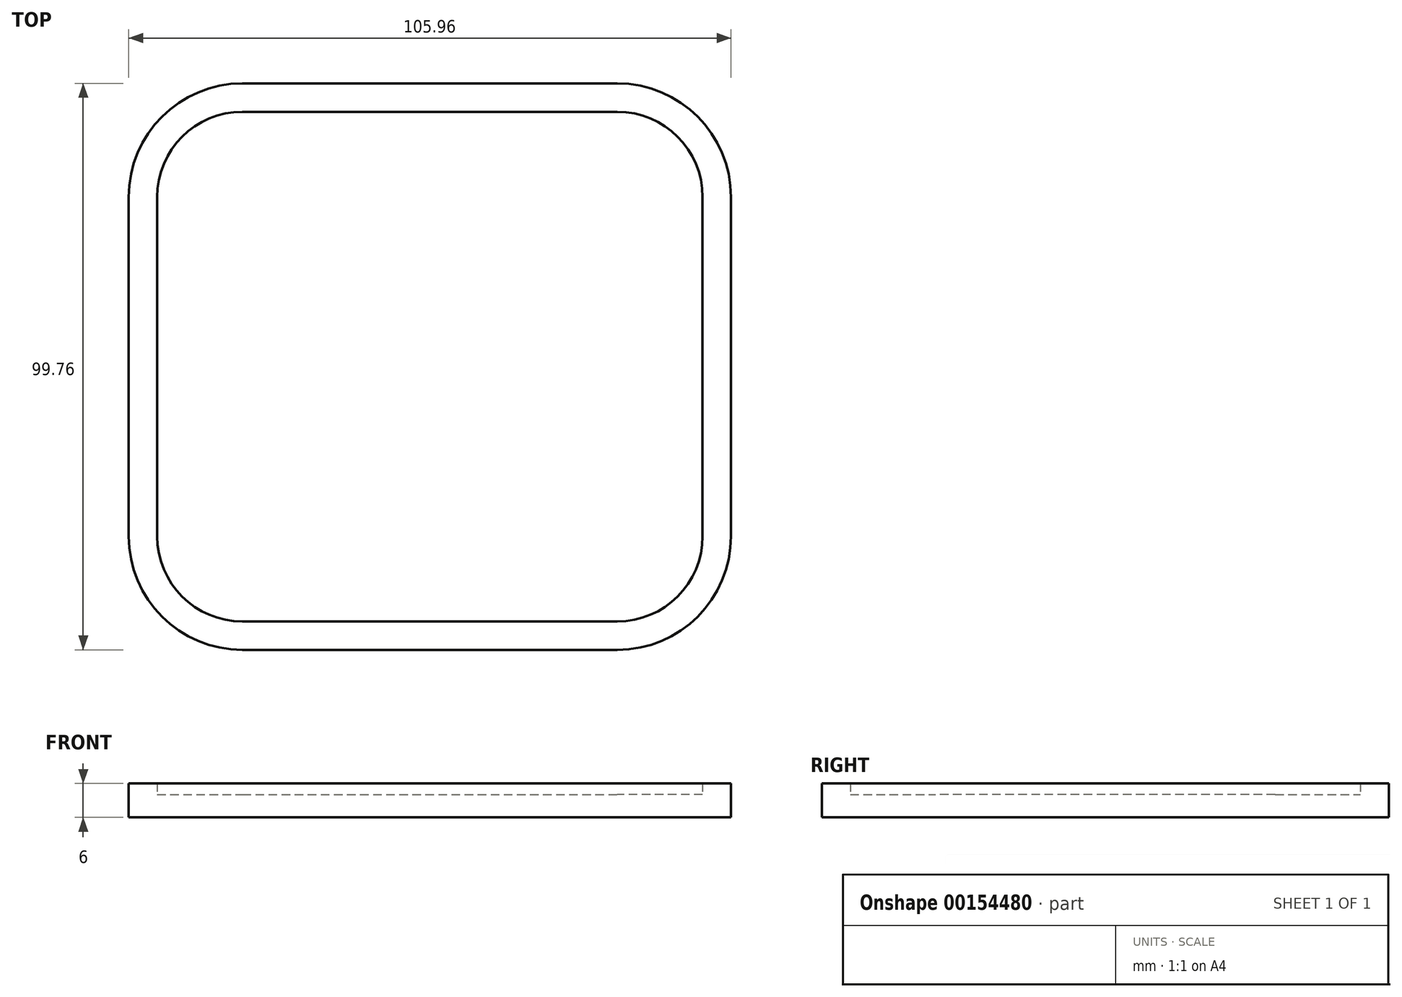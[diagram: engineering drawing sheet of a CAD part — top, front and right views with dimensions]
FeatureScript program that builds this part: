
annotation { "Feature Type Name" : "Feature", "Feature Type Description" : "" }
export const myFeature = defineFeature(function(context is Context, id is Id, definition is map)
    precondition{}
    {
        {
            var Q0;
            Q0=qCreatedBy(makeId("Top.planeOp"),FACE);
            var sketch = newSketch(context, id + "F0", { "sketchPlane" : qUnion([Q0])});
            skLineSegment(sketch, "E0.bottom", {"start": v(-32.98, 44.88) * mm, "end": v(32.98, 44.88) * mm});
            skLineSegment(sketch, "E0.top", {"start": v(-32.98, -44.88) * mm, "end": v(32.98, -44.88) * mm});
            skLineSegment(sketch, "E0.left", {"start": v(-47.98, 29.88) * mm, "end": v(-47.98, -29.88) * mm});
            skLineSegment(sketch, "E0.right", {"start": v(47.98, 29.88) * mm, "end": v(47.98, -29.88) * mm});
            skPoint(sketch, "E0.middle", {"position": v(0, 0) * mm});
            skPoint(sketch, "E1.visualSharp", {"position": v(-47.98, 44.88) * mm});
            skArc(sketch, "E1.filletArc", {"start": v(-32.98, 44.88) * mm, "mid": v(-43.59, 40.49) * mm, "end": v(-47.98, 29.88) * mm});
            skPoint(sketch, "E2.visualSharp", {"position": v(47.98, 44.88) * mm});
            skArc(sketch, "E2.filletArc", {"start": v(47.98, 29.88) * mm, "mid": v(43.59, 40.49) * mm, "end": v(32.98, 44.88) * mm});
            skPoint(sketch, "E3.visualSharp", {"position": v(47.98, -44.88) * mm});
            skArc(sketch, "E3.filletArc", {"start": v(32.98, -44.88) * mm, "mid": v(43.59, -40.49) * mm, "end": v(47.98, -29.88) * mm});
            skPoint(sketch, "E4.visualSharp", {"position": v(-47.98, -44.88) * mm});
            skArc(sketch, "E4.filletArc", {"start": v(-47.98, -29.88) * mm, "mid": v(-43.59, -40.49) * mm, "end": v(-32.98, -44.88) * mm});
            skLineSegment(sketch, "E5.0", {"start": v(-32.98, 49.88) * mm, "end": v(32.98, 49.88) * mm});
            skArc(sketch, "E5.1", {"start": v(52.98, 29.88) * mm, "mid": v(47.13, 44.02) * mm, "end": v(32.98, 49.88) * mm});
            skArc(sketch, "E5.2", {"start": v(-32.98, 49.88) * mm, "mid": v(-47.13, 44.02) * mm, "end": v(-52.98, 29.88) * mm});
            skLineSegment(sketch, "E5.3", {"start": v(52.98, 29.88) * mm, "end": v(52.98, -29.88) * mm});
            skLineSegment(sketch, "E5.4", {"start": v(-52.98, 29.88) * mm, "end": v(-52.98, -29.88) * mm});
            skArc(sketch, "E5.5", {"start": v(-52.98, -29.88) * mm, "mid": v(-47.13, -44.02) * mm, "end": v(-32.98, -49.88) * mm});
            skLineSegment(sketch, "E5.6", {"start": v(-32.98, -49.88) * mm, "end": v(32.98, -49.88) * mm});
            skArc(sketch, "E5.7", {"start": v(32.98, -49.88) * mm, "mid": v(47.13, -44.02) * mm, "end": v(52.98, -29.88) * mm});
            skSolve(sketch);
        }
        {
            var Q0;
            Q0=makeQuery(id+"F0.imprint","IMPRINT",FACE,{"disambiguationData":[TD([[makeQuery(id+"F0.imprint","IMPRINT",EDGE,{"derivedFrom":sQuery(id+"F0.wireOp",EDGE,"E0.bottom")}),-1.0]])]});
            extrude(context, id + "F1", {"entities" : qUnion([Q0]), "depth" : 4 * mm});
        }
        {
            var Q0;
            Q0=qSketchRegion(id+"F0",true);
            extrude(context, id + "F2", {"entities" : qUnion([Q0]), "operationType" : NewBodyOperationType.ADD, "depth" : 6 * mm});
        }
    });
